# Revit family: ShowerHead-1F-BuiltIn-Vitra-LiquidSeries-A42796
name_source: partatom
category: Plumbing Fixtures
revit_build: Autodesk Revit 2017 (Build: 20160225_1515(x64)
units: mm (PartAtom-declared; Revit-internal decimal feet)

## family parameters
Cut with Voids When Loaded = No
Host = Face
OmniClass Number = 23.45.00.00
OmniClass Title = Sanitary, Laundry, and Cleaning Equipment
Part Type = Normal
Room Calculation Point = No
Round Connector Dimension = Use Diameter
Shared = Yes

## types (2) — shared parameters
BIMobject category = Bath/Shower Mixer
Brand = VitrA
CW Connection = Yes
Connection Diameter (mm) = 15 mm  [stored 0.0492126 ft]
Description = Liquid 1F Built-in Showerhead
Design country = Turkey
HW Connection = Yes
IFC Classification = Sanitary Terminal
Main Material = Metal
Manufacturer = Vitra
Manufacturer name = Vitra
Masterformat 2014 Code = 22 41 23
Masterformat 2014 Description = Residential Showers
Mounting type = Wall Mounted
NBS Referans Code = 35-06-81
NBS Referans Description = Shower Heads
Nominal Depth (mm) = 130 mm  [stored 0.426509 ft]
Nominal Height (mm) = 955 mm  [stored 3.1332 ft]
Nominal Width (mm) = 90 mm
Number Of Connections = 1
OmniClass Code = 23-31 17 19
OmniClass Description = Shower Head Fixtures
Product Type = Showerhead
Product certification = https://www.vitraglobal.com
Product family = Liquid Series
Product group = Showers Head
Product url = https://www.vitraglobal.com
Technical description = https://www.vitraglobal.com
URL = https://vitraglobal.com
Uniclass 1.4 Code = L7214
Uniclass 1.4 Description = Showers
Uniclass 2.0 Code = PR-35-06-81
Uniclass 2.0 Description = Shower Heads
Uniclass 2015 Code = Pr_40_20_87_76
Uniclass 2015 Name = Shower heads
Uniformat II Code = D2010
Uniformat II Description = Plumbing Fixtures
Vent Connection = No
Warranty Period (Year) = 5 Years
Waste Connection = No
Weight Net (kg) = 2
Youtube = https://www.youtube.com
zero-valued in all types: Default Elevation

## per-type parameters (varying)
| type | Article No. (default) | Coating Material | Color | Model | Product SKU |
| ShowerHead-1F-BuiltIn-Vitra-LiquidSeries-A42796 | A42796 | Chrome (Metal) | Chrome | A42796 | A42796 |
| ShowerHead-1F-BuiltIn-Vitra-LiquidSeries-A4279639 | A4279639 | Glossy black (Metal) | Glossy black | A4279639 | A4279639 |

note: [stored X ft] marks values corroborated as IEEE doubles in the binary element streams (Revit-internal decimal feet)

## geometry (parser evidence)
native form markers: Sweep x1
no freeform markers — native parametric forms only
